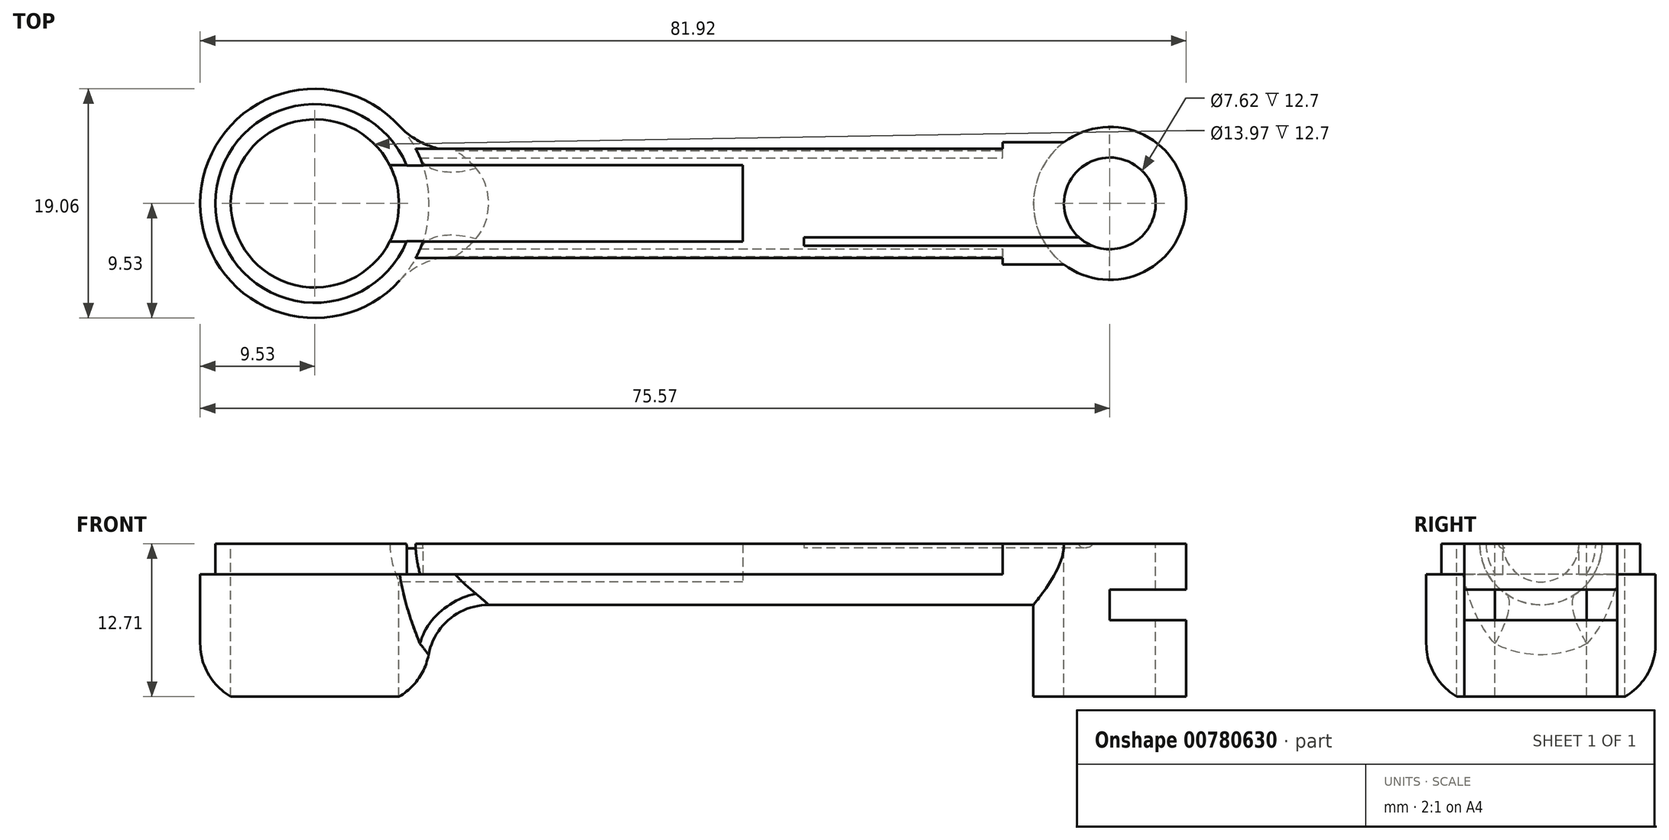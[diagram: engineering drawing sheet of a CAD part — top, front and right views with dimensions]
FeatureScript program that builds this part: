
annotation { "Feature Type Name" : "Feature", "Feature Type Description" : "" }
export const myFeature = defineFeature(function(context is Context, id is Id, definition is map)
    precondition{}
    {
        {
            var Q0;
            Q0=qCreatedBy(makeId("Top.planeOp"),FACE);
            var sketch = newSketch(context, id + "F0", { "sketchPlane" : qUnion([Q0])});
            skCircle(sketch, "E0", {"center": v(0, 0) * mm, "radius": 9.53 * mm});
            skSolve(sketch);
        }
        {
            var Q0;
            Q0=makeQuery(id+"F0.imprint","IMPRINT",FACE,{"disambiguationData":[TD([[makeQuery(id+"F0.imprint","IMPRINT",EDGE,{"derivedFrom":sQuery(id+"F0.wireOp",EDGE,"E0")}),1.0]])]});
            extrude(context, id + "F1", {"entities" : qUnion([Q0]), "depth" : 25.4 * mm, "offsetDistance" : 25.4 * mm});
        }
        {
            var Q0;
            Q0=makeQuery(id+"F1.opExtrude","CAP_FACE",FACE,{"disambiguationData":[OSD([sQuery(id+"F0.wireOp",EDGE,"E0")])],"isStart":false});
            var sketch = newSketch(context, id + "F2", { "sketchPlane" : qUnion([Q0])});
            skCircle(sketch, "E1", {"center": v(0, 0) * mm, "radius": 6.99 * mm});
            skSolve(sketch);
        }
        {
            var Q0;
            Q0=qCreatedBy(makeId("Right.planeOp"),FACE);
            var sketch = newSketch(context, id + "F3", { "sketchPlane" : qUnion([Q0])});
            skCircle(sketch, "E2", {"center": v(0, 15.88) * mm, "radius": 3.18 * mm});
            skSolve(sketch);
        }
        {
            var Q0;
            Q0=qSketchRegion(id+"F3",true);
            extrude(context, id + "F4", {"entities" : qUnion([Q0]), "operationType" : NewBodyOperationType.REMOVE, "depth" : 12.7 * mm, "offsetDistance" : 25.4 * mm});
        }
        {
            var Q0;
            Q0=qCreatedBy(makeId("Right.planeOp"),FACE);
            var sketch = newSketch(context, id + "F5", { "sketchPlane" : qUnion([Q0])});
            skLineSegment(sketch, "E3.top", {"start": v(9.53, 15.88) * mm, "end": v(-9.53, 15.88) * mm});
            skPoint(sketch, "E3.middle", {"position": v(0, 7.94) * mm});
            skLineSegment(sketch, "E4", {"start": v(-9.53, 15.88) * mm, "end": v(-9.53, 28.58) * mm});
            skLineSegment(sketch, "E5", {"start": v(9.53, 15.88) * mm, "end": v(9.53, 28.58) * mm});
            skLineSegment(sketch, "E6", {"start": v(-9.53, 28.58) * mm, "end": v(9.53, 28.58) * mm});
            skSolve(sketch);
        }
        {
            var Q0;
            Q0=qSketchRegion(id+"F5",true);
            extrude(context, id + "F6", {"entities" : qUnion([Q0]), "operationType" : NewBodyOperationType.REMOVE, "oppositeDirection" : true, "depth" : 25.4 * mm, "offsetDistance" : 25.4 * mm, "symmetric" : true});
        }
        {
            var Q0;
            Q0=qCreatedBy(makeId("Right.planeOp"),FACE);
            var sketch = newSketch(context, id + "F7", { "sketchPlane" : qUnion([Q0])});
            skArc(sketch, "E7", {"start": v(3.18, 15.88) * mm, "mid": v(0, 12.7) * mm, "end": v(-3.18, 15.88) * mm});
            skArc(sketch, "E8", {"start": v(-3.15, 18.42) * mm, "mid": v(-3.82, 17.22) * mm, "end": v(-4.05, 15.88) * mm});
            skArc(sketch, "E9", {"start": v(3.15, 18.42) * mm, "mid": v(3.82, 17.22) * mm, "end": v(4.05, 15.88) * mm});
            skLineSegment(sketch, "E10", {"start": v(-3.15, 18.42) * mm, "end": v(-4.4, 18.42) * mm});
            skLineSegment(sketch, "E11", {"start": v(3.15, 18.42) * mm, "end": v(4.4, 18.42) * mm});
            skLineSegment(sketch, "E12", {"start": v(-3.18, 15.88) * mm, "end": v(-4.05, 15.88) * mm});
            skLineSegment(sketch, "E13", {"start": v(3.18, 15.88) * mm, "end": v(4.05, 15.88) * mm});
            skArc(sketch, "E14", {"start": v(-4.4, 18.42) * mm, "mid": v(0, 10.8) * mm, "end": v(4.4, 18.42) * mm});
            skSolve(sketch);
        }
        {
            var Q0;
            Q0=qSketchRegion(id+"F7",true);
            var Q1;
            Q1=qConstructionFilter(qBodyType(qCreatedBy(id+"F7",EDGE),BodyType.WIRE),ConstructionObject.NO);
            extrude(context, id + "F8", {"entities" : qUnion([Q0]), "operationType" : NewBodyOperationType.ADD, "surfaceEntities" : qUnion([Q1]), "depth" : 38.1 * mm, "offsetDistance" : 25.4 * mm});
        }
        {
            var Q0;
            Q0=makeQuery(id+"F2.imprint","IMPRINT",FACE,{"disambiguationData":[TD([[makeQuery(id+"F2.imprint","IMPRINT",EDGE,{"derivedFrom":sQuery(id+"F2.wireOp",EDGE,"E1")}),1.0]])]});
            extrude(context, id + "F9", {"entities" : qUnion([Q0]), "operationType" : NewBodyOperationType.REMOVE, "oppositeDirection" : true, "depth" : 12.7 * mm, "offsetDistance" : 25.4 * mm});
        }
        {
            var Q0;
            Q0=makeQuery(id+"F8.opExtrude","CAP_FACE",FACE,{"disambiguationData":[OSD([sQuery(id+"F7.wireOp",EDGE,"E7"),sQuery(id+"F7.wireOp",EDGE,"E8"),sQuery(id+"F7.wireOp",EDGE,"E9"),sQuery(id+"F7.wireOp",EDGE,"E10"),sQuery(id+"F7.wireOp",EDGE,"E11"),sQuery(id+"F7.wireOp",EDGE,"E12"),sQuery(id+"F7.wireOp",EDGE,"E13"),sQuery(id+"F7.wireOp",EDGE,"E14")])],"isStart":false});
            var sketch = newSketch(context, id + "F10", { "sketchPlane" : qUnion([Q0])});
            skArc(sketch, "E15", {"start": v(-5.08, 15.88) * mm, "mid": v(0, 10.8) * mm, "end": v(5.08, 15.88) * mm});
            skArc(sketch, "E16", {"start": v(-3.53, 15.88) * mm, "mid": v(-3.18, 15.52) * mm, "end": v(-2.82, 15.88) * mm});
            skLineSegment(sketch, "E17", {"start": v(5.08, 15.88) * mm, "end": v(-2.82, 15.88) * mm});
            skLineSegment(sketch, "E18", {"start": v(-3.53, 15.88) * mm, "end": v(-5.08, 15.88) * mm});
            skSolve(sketch);
        }
        {
            var Q0;
            Q0=qSketchRegion(id+"F10",true);
            extrude(context, id + "F11", {"entities" : qUnion([Q0]), "operationType" : NewBodyOperationType.ADD, "depth" : 24.13 * mm, "offsetDistance" : 25.4 * mm});
        }
        {
            var Q0;
            Q0=makeQuery(id+"F1.opExtrude","CAP_FACE",FACE,{"disambiguationData":[OSD([sQuery(id+"F0.wireOp",EDGE,"E0")])],"isStart":true});
            var sketch = newSketch(context, id + "F12", { "sketchPlane" : qUnion([Q0])});
            skCircle(sketch, "E19", {"center": v(-3.18, 3.18) * mm, "radius": 0.95 * mm});
            skCircle(sketch, "E20", {"center": v(3.18, 3.18) * mm, "radius": 0.95 * mm});
            skCircle(sketch, "E21", {"center": v(3.18, -3.18) * mm, "radius": 0.95 * mm});
            skCircle(sketch, "E22", {"center": v(-3.18, -3.18) * mm, "radius": 0.95 * mm});
            skSolve(sketch);
        }
        {
            var Q0;
            Q0=qSketchRegion(id+"F12",true);
            extrude(context, id + "F13", {"entities" : qUnion([Q0]), "operationType" : NewBodyOperationType.REMOVE, "oppositeDirection" : true, "depth" : 25.4 * mm, "offsetDistance" : 25.4 * mm});
        }
        {
            var Q0;
            Q0=makeQuery(id+"F1.opExtrude","CAP_FACE",FACE,{"disambiguationData":[OSD([sQuery(id+"F0.wireOp",EDGE,"E0")])],"isStart":true});
            var sketch = newSketch(context, id + "F14", { "sketchPlane" : qUnion([Q0])});
            skCircle(sketch, "E23", {"center": v(0, 0) * mm, "radius": 6.99 * mm});
            skSolve(sketch);
        }
        {
            var Q0;
            Q0=qSketchRegion(id+"F14",true);
            extrude(context, id + "F15", {"entities" : qUnion([Q0]), "operationType" : NewBodyOperationType.REMOVE, "oppositeDirection" : true, "depth" : 7.62 * mm, "offsetDistance" : 25.4 * mm});
        }
        {
            var Q0;
            Q0=makeQuery(id+"F9.boolean.opBoolean","SPLIT",FACE,{"disambiguationData":[TD([makeQuery(id+"F1.opExtrude","SWEPT_FACE",FACE,{"disambiguationData":[OSD([sQuery(id+"F0.wireOp",EDGE,"E0")])]})])],"derivedFrom":makeQuery(id+"F8.boolean.opBoolean","MERGE",FACE,{"derivedFrom":[makeQuery(id+"F6.boolean.opBoolean","COPY",FACE,{"derivedFrom":makeQuery(id+"F6.opExtrude","SWEPT_FACE",FACE,{"disambiguationData":[OSD([sQuery(id+"F5.wireOp",EDGE,"E3.top")])]})}),makeQuery(id+"F8.opExtrude","SWEPT_FACE",FACE,{"disambiguationData":[OSD([sQuery(id+"F7.wireOp",EDGE,"E12")])]}),makeQuery(id+"F8.opExtrude","SWEPT_FACE",FACE,{"disambiguationData":[OSD([sQuery(id+"F7.wireOp",EDGE,"E13")])]})]})});
            var sketch = newSketch(context, id + "F16", { "sketchPlane" : qUnion([Q0])});
            skCircle(sketch, "E24", {"center": v(0, 0) * mm, "radius": 6.99 * mm});
            skCircle(sketch, "E25", {"center": v(0, 0) * mm, "radius": 8.26 * mm});
            skSolve(sketch);
        }
        {
            var Q0;
            Q0=qSketchRegion(id+"F16",true);
            extrude(context, id + "F17", {"entities" : qUnion([Q0]), "operationType" : NewBodyOperationType.REMOVE, "depth" : 25.4 * mm, "offsetDistance" : 25.4 * mm});
        }
        {
            var Q0;
            Q0=makeQuery(id+"F8.opExtrude","SWEPT_FACE",FACE,{"disambiguationData":[OSD([sQuery(id+"F7.wireOp",EDGE,"E11")])]});
            var sketch = newSketch(context, id + "F18", { "sketchPlane" : qUnion([Q0])});
            skArc(sketch, "E26", {"start": v(7.63, 3.15) * mm, "mid": v(-8.25, 0) * mm, "end": v(7.63, -3.15) * mm});
            skArc(sketch, "E27", {"start": v(8.99, 3.15) * mm, "mid": v(-9.53, 0) * mm, "end": v(8.99, -3.15) * mm});
            skLineSegment(sketch, "E28", {"start": v(7.63, 3.15) * mm, "end": v(8.99, 3.15) * mm});
            skLineSegment(sketch, "E29", {"start": v(7.63, -3.15) * mm, "end": v(8.99, -3.15) * mm});
            skSolve(sketch);
        }
        {
            var Q0;
            Q0=qSketchRegion(id+"F18",true);
            extrude(context, id + "F19", {"entities" : qUnion([Q0]), "operationType" : NewBodyOperationType.REMOVE, "oppositeDirection" : true, "depth" : 5.08 * mm, "offsetDistance" : 25.4 * mm});
        }
        {
            var Q0;
            {var subQ0=sQuery(id+"F7.wireOp",EDGE,"E10");var subQ1=sQuery(id+"F7.wireOp",EDGE,"E8");var subQ2=sQuery(id+"F7.wireOp",EDGE,"E12");var subQ3=sQuery(id+"F7.wireOp",EDGE,"E13");var subQ4=sQuery(id+"F7.wireOp",EDGE,"E14");Q0=makeQuery(id+"F11.boolean.opBoolean","SPLIT",FACE,{"disambiguationData":[TD([makeQuery(id+"F8.opExtrude","SWEPT_FACE",FACE,{"disambiguationData":[OSD([subQ1])]})])],"derivedFrom":makeQuery(id+"F8.opExtrude","CAP_FACE",FACE,{"disambiguationData":[OSD([sQuery(id+"F7.wireOp",EDGE,"E7"),subQ1,sQuery(id+"F7.wireOp",EDGE,"E9"),subQ0,sQuery(id+"F7.wireOp",EDGE,"E11"),subQ2,subQ3,subQ4])],"isStart":false})});}
            var sketch = newSketch(context, id + "F20", { "sketchPlane" : qUnion([Q0])});
            skArc(sketch, "E30", {"start": v(-4.05, 15.88) * mm, "mid": v(0, 19.92) * mm, "end": v(4.05, 15.88) * mm});
            skLineSegment(sketch, "E31", {"start": v(-4.05, 15.88) * mm, "end": v(4.05, 15.88) * mm});
            skSolve(sketch);
        }
        {
            var Q0;
            Q0=qSketchRegion(id+"F20",true);
            extrude(context, id + "F21", {"entities" : qUnion([Q0]), "operationType" : NewBodyOperationType.REMOVE, "oppositeDirection" : true, "depth" : 63.5 * mm, "offsetDistance" : 25.4 * mm});
        }
        {
            var Q0;
            {var subQ0=sQuery(id+"F7.wireOp",EDGE,"E10");var subQ1=sQuery(id+"F7.wireOp",EDGE,"E8");var subQ2=sQuery(id+"F7.wireOp",EDGE,"E12");var subQ3=sQuery(id+"F7.wireOp",EDGE,"E13");var subQ4=sQuery(id+"F7.wireOp",EDGE,"E14");Q0=makeQuery(id+"F11.boolean.opBoolean","SPLIT",FACE,{"disambiguationData":[TD([makeQuery(id+"F8.opExtrude","SWEPT_FACE",FACE,{"disambiguationData":[OSD([subQ1])]})])],"derivedFrom":makeQuery(id+"F8.opExtrude","CAP_FACE",FACE,{"disambiguationData":[OSD([sQuery(id+"F7.wireOp",EDGE,"E7"),subQ1,sQuery(id+"F7.wireOp",EDGE,"E9"),subQ0,sQuery(id+"F7.wireOp",EDGE,"E11"),subQ2,subQ3,subQ4])],"isStart":false})});}
            var sketch = newSketch(context, id + "F22", { "sketchPlane" : qUnion([Q0])});
            skArc(sketch, "E32", {"start": v(-3.78, 13.34) * mm, "mid": v(-4.35, 14.55) * mm, "end": v(-4.55, 15.88) * mm});
            skLineSegment(sketch, "E33", {"start": v(-3.78, 13.34) * mm, "end": v(-4.4, 13.34) * mm});
            skArc(sketch, "E34", {"start": v(-3.15, 18.42) * mm, "mid": v(-3.82, 17.22) * mm, "end": v(-4.05, 15.88) * mm});
            skLineSegment(sketch, "E35", {"start": v(-4.55, 15.88) * mm, "end": v(-4.05, 15.88) * mm});
            skLineSegment(sketch, "E36", {"start": v(-3.15, 18.42) * mm, "end": v(-4.4, 18.42) * mm});
            skArc(sketch, "E37", {"start": v(-4.4, 13.34) * mm, "mid": v(-5.08, 15.88) * mm, "end": v(-4.4, 18.42) * mm});
            skSolve(sketch);
        }
        {
            var Q0;
            Q0 = qSketchRegion(id + "F22", true);
            extrude(context, id + "F23", {"entities" : qUnion([Q0]), "operationType" : NewBodyOperationType.REMOVE, "oppositeDirection" : true, "depth" : 30.48 * mm, "offsetDistance" : 25.4 * mm});
        }
        {
            var Q0;
            {var subQ0=sQuery(id+"F7.wireOp",EDGE,"E11");var subQ1=sQuery(id+"F7.wireOp",EDGE,"E9");var subQ2=sQuery(id+"F7.wireOp",EDGE,"E12");var subQ3=sQuery(id+"F7.wireOp",EDGE,"E13");var subQ4=sQuery(id+"F7.wireOp",EDGE,"E14");Q0=makeQuery(id+"F11.boolean.opBoolean","SPLIT",FACE,{"disambiguationData":[TD([makeQuery(id+"F8.opExtrude","SWEPT_FACE",FACE,{"disambiguationData":[OSD([subQ1])]})])],"derivedFrom":makeQuery(id+"F8.opExtrude","CAP_FACE",FACE,{"disambiguationData":[OSD([sQuery(id+"F7.wireOp",EDGE,"E7"),sQuery(id+"F7.wireOp",EDGE,"E8"),subQ1,sQuery(id+"F7.wireOp",EDGE,"E10"),subQ0,subQ2,subQ3,subQ4])],"isStart":false})});}
            var sketch = newSketch(context, id + "F24", { "sketchPlane" : qUnion([Q0])});
            skArc(sketch, "E38", {"start": v(3.78, 13.34) * mm, "mid": v(4.35, 14.55) * mm, "end": v(4.55, 15.88) * mm});
            skLineSegment(sketch, "E39", {"start": v(4.55, 15.88) * mm, "end": v(4.05, 15.88) * mm});
            skArc(sketch, "E40", {"start": v(4.05, 15.88) * mm, "mid": v(3.82, 17.22) * mm, "end": v(3.15, 18.42) * mm});
            skLineSegment(sketch, "E41", {"start": v(3.15, 18.42) * mm, "end": v(4.4, 18.42) * mm});
            skLineSegment(sketch, "E42", {"start": v(3.78, 13.34) * mm, "end": v(4.4, 13.34) * mm});
            skArc(sketch, "E43", {"start": v(4.4, 13.34) * mm, "mid": v(5.08, 15.88) * mm, "end": v(4.4, 18.42) * mm});
            skSolve(sketch);
        }
        {
            var Q0;
            Q0 = qSketchRegion(id + "F24", true);
            extrude(context, id + "F25", {"entities" : qUnion([Q0]), "operationType" : NewBodyOperationType.REMOVE, "oppositeDirection" : true, "depth" : 30.48 * mm, "offsetDistance" : 25.4 * mm});
        }
        {
            var Q0;
            Q0=qCreatedBy(makeId("Right.planeOp"),FACE);
            var sketch = newSketch(context, id + "F26", { "sketchPlane" : qUnion([Q0])});
            skLineSegment(sketch, "E44.bottom", {"start": v(-9.53, 0) * mm, "end": v(9.53, 0) * mm});
            skLineSegment(sketch, "E44.top", {"start": v(-9.53, 3.17) * mm, "end": v(9.53, 3.17) * mm});
            skLineSegment(sketch, "E44.left", {"start": v(-9.53, 0) * mm, "end": v(-9.53, 3.17) * mm});
            skLineSegment(sketch, "E44.right", {"start": v(9.53, 0) * mm, "end": v(9.53, 3.17) * mm});
            skSolve(sketch);
        }
        {
            var Q0;
            Q0 = qSketchRegion(id + "F26", true);
            extrude(context, id + "F27", {"entities" : qUnion([Q0]), "operationType" : NewBodyOperationType.REMOVE, "oppositeDirection" : true, "depth" : 25.4 * mm, "offsetDistance" : 25.4 * mm, "symmetric" : true});
        }
        {
            var Q0;
            Q0=makeQuery(id+"F15.boolean.opBoolean","COPY",FACE,{"derivedFrom":makeQuery(id+"F15.opExtrude","CAP_FACE",FACE,{"disambiguationData":[OSD([sQuery(id+"F14.wireOp",EDGE,"E23")])],"isStart":false})});
            var sketch = newSketch(context, id + "F28", { "sketchPlane" : qUnion([Q0])});
            skCircle(sketch, "E45", {"center": v(0, 0) * mm, "radius": 6.99 * mm});
            skSolve(sketch);
        }
        {
            var Q0;
            Q0 = qSketchRegion(id + "F28", true);
            extrude(context, id + "F29", {"entities" : qUnion([Q0]), "operationType" : NewBodyOperationType.REMOVE, "oppositeDirection" : true, "depth" : 25.4 * mm, "offsetDistance" : 25.4 * mm});
        }
        {
            var Q0;
            Q0=makeQuery(id+"F27.boolean.opBoolean","INTERSECT",EDGE,{"derivedFrom":[makeQuery(id+"F1.opExtrude","SWEPT_FACE",FACE,{"disambiguationData":[OSD([sQuery(id+"F0.wireOp",EDGE,"E0")])]}),makeQuery(id+"F27.opExtrude","SWEPT_FACE",FACE,{"disambiguationData":[OSD([sQuery(id+"F26.wireOp",EDGE,"E44.top")])]})]});
            fillet(context, id + "F30", {"entities" : qUnion([Q0]), "radius" : 5.08 * mm, "tangentPropagation" : true, "allowEdgeOverflow" : false});
        }
        {
            var Q0;
            Q0=makeQuery(id+"F19.boolean.opBoolean","SPLIT",EDGE,{"derivedFrom":makeQuery(id+"F8.boolean.opBoolean","INTERSECT",EDGE,{"derivedFrom":[makeQuery(id+"F1.opExtrude","SWEPT_FACE",FACE,{"disambiguationData":[OSD([sQuery(id+"F0.wireOp",EDGE,"E0")])]}),makeQuery(id+"F8.opExtrude","SWEPT_FACE",FACE,{"disambiguationData":[OSD([sQuery(id+"F7.wireOp",EDGE,"E14")])]})]})});
            fillet(context, id + "F31", {"entities" : qUnion([Q0]), "radius" : 5.08 * mm, "tangentPropagation" : true, "allowEdgeOverflow" : false});
        }
        {
            var Q0;
            {var subQ0=sQuery(id+"F7.wireOp",EDGE,"E9");var subQ1=makeQuery(id+"F8.opExtrude","SWEPT_FACE",FACE,{"disambiguationData":[OSD([subQ0])]});var subQ2=sQuery(id+"F10.wireOp",EDGE,"aL0u9GlF-6Q7s-W1V7-4wS0-8lCQG8VcdnJv");var subQ3=sQuery(id+"F10.wireOp",EDGE,"2Tc0jqr0-cNR8-OvJQ-WwAY-mDO75ud9QsQn");var subQ7=sQuery(id+"F7.wireOp",EDGE,"E13");var subQ8=sQuery(id+"F7.wireOp",EDGE,"E12");var subQ9=sQuery(id+"F7.wireOp",EDGE,"E8");var subQ16=makeQuery(id+"F8.boolean.opBoolean","MERGE",FACE,{"derivedFrom":[makeQuery(id+"F6.boolean.opBoolean","COPY",FACE,{"derivedFrom":makeQuery(id+"F6.opExtrude","SWEPT_FACE",FACE,{"disambiguationData":[OSD([sQuery(id+"F5.wireOp",EDGE,"E3.top")])]})}),makeQuery(id+"F8.opExtrude","SWEPT_FACE",FACE,{"disambiguationData":[OSD([subQ8])]}),makeQuery(id+"F8.opExtrude","SWEPT_FACE",FACE,{"disambiguationData":[OSD([subQ7])]})]});Q0=makeQuery(id+"F25.boolean.opBoolean","MERGE",FACE,{"derivedFrom":[makeQuery(id+"F19.boolean.opBoolean","SPLIT",FACE,{"disambiguationData":[TD([subQ1])],"derivedFrom":makeQuery(id+"F17.boolean.opBoolean","MERGE",FACE,{"derivedFrom":[makeQuery(id+"F9.boolean.opBoolean","SPLIT",FACE,{"disambiguationData":[TD([makeQuery(id+"F1.opExtrude","SWEPT_FACE",FACE,{"disambiguationData":[OSD([sQuery(id+"F0.wireOp",EDGE,"E0")])]})])],"derivedFrom":subQ16}),makeQuery(id+"F11.boolean.opBoolean","MERGE",FACE,{"derivedFrom":[makeQuery(id+"F9.boolean.opBoolean","SPLIT",FACE,{"disambiguationData":[TD([makeQuery(id+"F8.opExtrude","SWEPT_FACE",FACE,{"disambiguationData":[OSD([subQ9])]})])],"derivedFrom":subQ16}),makeQuery(id+"F11.opExtrude","SWEPT_FACE",FACE,{"disambiguationData":[OSD([subQ2])]})]}),makeQuery(id+"F11.boolean.opBoolean","MERGE",FACE,{"derivedFrom":[makeQuery(id+"F9.boolean.opBoolean","SPLIT",FACE,{"disambiguationData":[TD([subQ1])],"derivedFrom":subQ16}),makeQuery(id+"F11.opExtrude","SWEPT_FACE",FACE,{"disambiguationData":[OSD([subQ3])]})]}),makeQuery(id+"F17.opExtrude","CAP_FACE",FACE,{"disambiguationData":[OSD([sQuery(id+"F16.wireOp",EDGE,"E24"),sQuery(id+"F16.wireOp",EDGE,"E25")])],"isStart":true})]})}),makeQuery(id+"F25.opExtrude","SWEPT_FACE",FACE,{"disambiguationData":[OSD([sQuery(id+"F24.wireOp",EDGE,"E39")])]})]});}
            var sketch = newSketch(context, id + "F32", { "sketchPlane" : qUnion([Q0])});
            skCircle(sketch, "E46", {"center": v(66.04, 0) * mm, "radius": 3.81 * mm});
            skCircle(sketch, "E47", {"center": v(66.04, 0) * mm, "radius": 6.35 * mm});
            skSolve(sketch);
        }
        {
            var Q0;
            Q0 = qSketchRegion(id + "F32", true);
            extrude(context, id + "F33", {"entities" : qUnion([Q0]), "operationType" : NewBodyOperationType.ADD, "oppositeDirection" : true, "depth" : 12.7 * mm, "offsetDistance" : 25.4 * mm});
        }
        {
            var Q0;
            Q0=makeQuery(id+"F11.opExtrude","CAP_FACE",FACE,{"disambiguationData":[OSD([sQuery(id+"F10.wireOp",EDGE,"E15"),sQuery(id+"F10.wireOp",EDGE,"00xkIltH-ur7c-vDCf-NMd2-okXEgH0ywGPR"),sQuery(id+"F10.wireOp",EDGE,"2Tc0jqr0-cNR8-OvJQ-WwAY-mDO75ud9QsQn"),sQuery(id+"F10.wireOp",EDGE,"aL0u9GlF-6Q7s-W1V7-4wS0-8lCQG8VcdnJv")])],"isStart":true});
            var sketch = newSketch(context, id + "F34", { "sketchPlane" : qUnion([Q0])});
            skArc(sketch, "E48", {"start": v(-3.18, 15.88) * mm, "mid": v(0, 12.7) * mm, "end": v(3.18, 15.88) * mm});
            skLineSegment(sketch, "E49", {"start": v(-3.18, 15.88) * mm, "end": v(3.18, 15.88) * mm});
            skSolve(sketch);
        }
        {
            var Q0;
            Q0 = qSketchRegion(id + "F34", true);
            extrude(context, id + "F35", {"entities" : qUnion([Q0]), "operationType" : NewBodyOperationType.ADD, "depth" : 2.54 * mm, "offsetDistance" : 25.4 * mm});
        }
        {
            var Q0;
            {var subQ0=sQuery(id+"F7.wireOp",EDGE,"E7");var subQ1=sQuery(id+"F7.wireOp",EDGE,"E12");var subQ4=sQuery(id+"F7.wireOp",EDGE,"E13");Q0=makeQuery(id+"F35.boolean.opBoolean","MERGE",FACE,{"derivedFrom":[makeQuery(id+"F11.boolean.opBoolean","SPLIT",FACE,{"disambiguationData":[TD([makeQuery(id+"F4.boolean.opBoolean","COPY",FACE,{"derivedFrom":makeQuery(id+"F4.opExtrude","SWEPT_FACE",FACE,{"disambiguationData":[OSD([sQuery(id+"F3.wireOp",EDGE,"E2")])]})})])],"derivedFrom":makeQuery(id+"F8.opExtrude","CAP_FACE",FACE,{"disambiguationData":[OSD([subQ0,sQuery(id+"F7.wireOp",EDGE,"E8"),sQuery(id+"F7.wireOp",EDGE,"E9"),sQuery(id+"F7.wireOp",EDGE,"E10"),sQuery(id+"F7.wireOp",EDGE,"E11"),subQ1,subQ4,sQuery(id+"F7.wireOp",EDGE,"E14")])],"isStart":false})}),makeQuery(id+"F35.opExtrude","CAP_FACE",FACE,{"disambiguationData":[OSD([sQuery(id+"F34.wireOp",EDGE,"E48"),sQuery(id+"F34.wireOp",EDGE,"E49")])],"isStart":true})]});}
            extrude(context, id + "F36", {"entities" : qUnion([Q0]), "operationType" : NewBodyOperationType.REMOVE, "depth" : 27.94 * mm, "offsetDistance" : 25.4 * mm});
        }
        {
            var Q0;
            Q0=makeQuery(id+"F23.boolean.opBoolean","COPY",FACE,{"derivedFrom":makeQuery(id+"F23.opExtrude","CAP_FACE",FACE,{"disambiguationData":[OSD([sQuery(id+"F22.wireOp",EDGE,"E32"),sQuery(id+"F22.wireOp",EDGE,"E33"),sQuery(id+"F22.wireOp",EDGE,"E34"),sQuery(id+"F22.wireOp",EDGE,"E35"),sQuery(id+"F22.wireOp",EDGE,"E36"),sQuery(id+"F22.wireOp",EDGE,"E37")])],"isStart":true})});
            extrude(context, id + "F37", {"entities" : qUnion([Q0]), "operationType" : NewBodyOperationType.REMOVE, "oppositeDirection" : true, "depth" : 19.05 * mm, "offsetDistance" : 25.4 * mm});
        }
        {
            var Q0;
            Q0=makeQuery(id+"F25.boolean.opBoolean","COPY",FACE,{"derivedFrom":makeQuery(id+"F25.opExtrude","CAP_FACE",FACE,{"disambiguationData":[OSD([sQuery(id+"F24.wireOp",EDGE,"E38"),sQuery(id+"F24.wireOp",EDGE,"E39"),sQuery(id+"F24.wireOp",EDGE,"E40"),sQuery(id+"F24.wireOp",EDGE,"E41"),sQuery(id+"F24.wireOp",EDGE,"E42"),sQuery(id+"F24.wireOp",EDGE,"E43")])],"isStart":true})});
            extrude(context, id + "F38", {"entities" : qUnion([Q0]), "operationType" : NewBodyOperationType.REMOVE, "oppositeDirection" : true, "depth" : 19.05 * mm, "offsetDistance" : 25.4 * mm});
        }
        {
            var Q0;
            {var subQ0=sQuery(id+"F7.wireOp",EDGE,"E9");var subQ1=makeQuery(id+"F8.opExtrude","SWEPT_FACE",FACE,{"disambiguationData":[OSD([subQ0])]});var subQ2=sQuery(id+"F10.wireOp",EDGE,"E18");var subQ3=sQuery(id+"F10.wireOp",EDGE,"E17");var subQ8=sQuery(id+"F7.wireOp",EDGE,"E13");var subQ9=sQuery(id+"F7.wireOp",EDGE,"E12");var subQ10=sQuery(id+"F7.wireOp",EDGE,"E8");var subQ20=makeQuery(id+"F8.boolean.opBoolean","MERGE",FACE,{"derivedFrom":[makeQuery(id+"F6.boolean.opBoolean","COPY",FACE,{"derivedFrom":makeQuery(id+"F6.opExtrude","SWEPT_FACE",FACE,{"disambiguationData":[OSD([sQuery(id+"F5.wireOp",EDGE,"E3.top")])]})}),makeQuery(id+"F8.opExtrude","SWEPT_FACE",FACE,{"disambiguationData":[OSD([subQ9])]}),makeQuery(id+"F8.opExtrude","SWEPT_FACE",FACE,{"disambiguationData":[OSD([subQ8])]})]});var subQ21=makeQuery(id+"F8.opExtrude","SWEPT_FACE",FACE,{"disambiguationData":[OSD([subQ10])]});var subQ22=makeQuery(id+"F17.boolean.opBoolean","MERGE",FACE,{"derivedFrom":[makeQuery(id+"F9.boolean.opBoolean","SPLIT",FACE,{"disambiguationData":[TD([makeQuery(id+"F1.opExtrude","SWEPT_FACE",FACE,{"disambiguationData":[OSD([sQuery(id+"F0.wireOp",EDGE,"E0")])]})])],"derivedFrom":subQ20}),makeQuery(id+"F11.boolean.opBoolean","MERGE",FACE,{"derivedFrom":[makeQuery(id+"F9.boolean.opBoolean","SPLIT",FACE,{"disambiguationData":[TD([subQ21])],"derivedFrom":subQ20}),makeQuery(id+"F11.opExtrude","SWEPT_FACE",FACE,{"disambiguationData":[OSD([subQ2])]})]}),makeQuery(id+"F11.boolean.opBoolean","MERGE",FACE,{"derivedFrom":[makeQuery(id+"F9.boolean.opBoolean","SPLIT",FACE,{"disambiguationData":[TD([subQ1])],"derivedFrom":subQ20}),makeQuery(id+"F11.opExtrude","SWEPT_FACE",FACE,{"disambiguationData":[OSD([subQ3])]})]}),makeQuery(id+"F17.opExtrude","CAP_FACE",FACE,{"disambiguationData":[OSD([sQuery(id+"F16.wireOp",EDGE,"E24"),sQuery(id+"F16.wireOp",EDGE,"E25")])],"isStart":true})]});Q0=makeQuery(id+"F35.boolean.opBoolean","MERGE",FACE,{"derivedFrom":[makeQuery(id+"F33.boolean.opBoolean","MERGE",FACE,{"derivedFrom":[makeQuery(id+"F23.boolean.opBoolean","MERGE",FACE,{"derivedFrom":[makeQuery(id+"F19.boolean.opBoolean","SPLIT",FACE,{"disambiguationData":[TD([subQ21])],"derivedFrom":subQ22}),makeQuery(id+"F23.opExtrude","SWEPT_FACE",FACE,{"disambiguationData":[OSD([sQuery(id+"F22.wireOp",EDGE,"E35")])]})]}),makeQuery(id+"F25.boolean.opBoolean","MERGE",FACE,{"derivedFrom":[makeQuery(id+"F19.boolean.opBoolean","SPLIT",FACE,{"disambiguationData":[TD([subQ1])],"derivedFrom":subQ22}),makeQuery(id+"F25.opExtrude","SWEPT_FACE",FACE,{"disambiguationData":[OSD([sQuery(id+"F24.wireOp",EDGE,"E39")])]})]}),makeQuery(id+"F33.opExtrude","CAP_FACE",FACE,{"disambiguationData":[OSD([sQuery(id+"F32.wireOp",EDGE,"E46"),sQuery(id+"F32.wireOp",EDGE,"E47")])],"isStart":true})]}),makeQuery(id+"F35.opExtrude","SWEPT_FACE",FACE,{"disambiguationData":[OSD([sQuery(id+"F34.wireOp",EDGE,"E49")])]})]});}
            var sketch = newSketch(context, id + "F39", { "sketchPlane" : qUnion([Q0])});
            skArc(sketch, "E50", {"start": v(66.04, 6.35) * mm, "mid": v(72.39, 0) * mm, "end": v(66.04, -6.35) * mm});
            skLineSegment(sketch, "E51", {"start": v(66.04, 6.35) * mm, "end": v(66.04, -6.35) * mm});
            skSolve(sketch);
        }
        {
            var Q0;
            Q0 = qSketchRegion(id + "F39", true);
            extrude(context, id + "F40", {"entities" : qUnion([Q0]), "operationType" : NewBodyOperationType.REMOVE, "oppositeDirection" : true, "depth" : 6.35 * mm, "offsetDistance" : 25.4 * mm});
        }
        {
            var Q0;
            {var subQ0=sQuery(id+"F7.wireOp",EDGE,"E9");var subQ1=makeQuery(id+"F8.opExtrude","SWEPT_FACE",FACE,{"disambiguationData":[OSD([subQ0])]});var subQ2=sQuery(id+"F10.wireOp",EDGE,"E18");var subQ3=sQuery(id+"F10.wireOp",EDGE,"E17");var subQ8=sQuery(id+"F7.wireOp",EDGE,"E13");var subQ9=sQuery(id+"F7.wireOp",EDGE,"E12");var subQ10=sQuery(id+"F7.wireOp",EDGE,"E8");var subQ20=makeQuery(id+"F8.boolean.opBoolean","MERGE",FACE,{"derivedFrom":[makeQuery(id+"F6.boolean.opBoolean","COPY",FACE,{"derivedFrom":makeQuery(id+"F6.opExtrude","SWEPT_FACE",FACE,{"disambiguationData":[OSD([sQuery(id+"F5.wireOp",EDGE,"E3.top")])]})}),makeQuery(id+"F8.opExtrude","SWEPT_FACE",FACE,{"disambiguationData":[OSD([subQ9])]}),makeQuery(id+"F8.opExtrude","SWEPT_FACE",FACE,{"disambiguationData":[OSD([subQ8])]})]});var subQ21=makeQuery(id+"F8.opExtrude","SWEPT_FACE",FACE,{"disambiguationData":[OSD([subQ10])]});var subQ22=makeQuery(id+"F17.boolean.opBoolean","MERGE",FACE,{"derivedFrom":[makeQuery(id+"F9.boolean.opBoolean","SPLIT",FACE,{"disambiguationData":[TD([makeQuery(id+"F1.opExtrude","SWEPT_FACE",FACE,{"disambiguationData":[OSD([sQuery(id+"F0.wireOp",EDGE,"E0")])]})])],"derivedFrom":subQ20}),makeQuery(id+"F11.boolean.opBoolean","MERGE",FACE,{"derivedFrom":[makeQuery(id+"F9.boolean.opBoolean","SPLIT",FACE,{"disambiguationData":[TD([subQ21])],"derivedFrom":subQ20}),makeQuery(id+"F11.opExtrude","SWEPT_FACE",FACE,{"disambiguationData":[OSD([subQ2])]})]}),makeQuery(id+"F11.boolean.opBoolean","MERGE",FACE,{"derivedFrom":[makeQuery(id+"F9.boolean.opBoolean","SPLIT",FACE,{"disambiguationData":[TD([subQ1])],"derivedFrom":subQ20}),makeQuery(id+"F11.opExtrude","SWEPT_FACE",FACE,{"disambiguationData":[OSD([subQ3])]})]}),makeQuery(id+"F17.opExtrude","CAP_FACE",FACE,{"disambiguationData":[OSD([sQuery(id+"F16.wireOp",EDGE,"E24"),sQuery(id+"F16.wireOp",EDGE,"E25")])],"isStart":true})]});Q0=makeQuery(id+"F35.boolean.opBoolean","MERGE",FACE,{"derivedFrom":[makeQuery(id+"F33.boolean.opBoolean","MERGE",FACE,{"derivedFrom":[makeQuery(id+"F23.boolean.opBoolean","MERGE",FACE,{"derivedFrom":[makeQuery(id+"F19.boolean.opBoolean","SPLIT",FACE,{"disambiguationData":[TD([subQ21])],"derivedFrom":subQ22}),makeQuery(id+"F23.opExtrude","SWEPT_FACE",FACE,{"disambiguationData":[OSD([sQuery(id+"F22.wireOp",EDGE,"E35")])]})]}),makeQuery(id+"F25.boolean.opBoolean","MERGE",FACE,{"derivedFrom":[makeQuery(id+"F19.boolean.opBoolean","SPLIT",FACE,{"disambiguationData":[TD([subQ1])],"derivedFrom":subQ22}),makeQuery(id+"F25.opExtrude","SWEPT_FACE",FACE,{"disambiguationData":[OSD([sQuery(id+"F24.wireOp",EDGE,"E39")])]})]}),makeQuery(id+"F33.opExtrude","CAP_FACE",FACE,{"disambiguationData":[OSD([sQuery(id+"F32.wireOp",EDGE,"E46"),sQuery(id+"F32.wireOp",EDGE,"E47")])],"isStart":true})]}),makeQuery(id+"F35.opExtrude","SWEPT_FACE",FACE,{"disambiguationData":[OSD([sQuery(id+"F34.wireOp",EDGE,"E49")])]})]});}
            var sketch = newSketch(context, id + "F41", { "sketchPlane" : qUnion([Q0])});
            skArc(sketch, "E52", {"start": v(64.58, 6.18) * mm, "mid": v(72.39, -0.02) * mm, "end": v(64.53, -6.17) * mm});
            skArc(sketch, "E53", {"start": v(65.21, 3.72) * mm, "mid": v(69.85, 0.08) * mm, "end": v(65.36, -3.75) * mm});
            skLineSegment(sketch, "E54", {"start": v(65.21, 3.72) * mm, "end": v(64.58, 6.18) * mm});
            skLineSegment(sketch, "E55", {"start": v(65.36, -3.75) * mm, "end": v(64.53, -6.17) * mm});
            skSolve(sketch);
        }
        {
            var Q0;
            Q0 = qSketchRegion(id + "F41", true);
            extrude(context, id + "F42", {"entities" : qUnion([Q0]), "operationType" : NewBodyOperationType.ADD, "oppositeDirection" : true, "depth" : 3.8 * mm, "offsetDistance" : 25.4 * mm});
        }
        {
            var Q0;
            {var subQ0=sQuery(id+"F7.wireOp",EDGE,"E7");var subQ1=sQuery(id+"F7.wireOp",EDGE,"E12");var subQ4=sQuery(id+"F7.wireOp",EDGE,"E13");Q0=makeQuery(id+"F35.boolean.opBoolean","MERGE",FACE,{"derivedFrom":[makeQuery(id+"F11.boolean.opBoolean","SPLIT",FACE,{"disambiguationData":[TD([makeQuery(id+"F4.boolean.opBoolean","COPY",FACE,{"derivedFrom":makeQuery(id+"F4.opExtrude","SWEPT_FACE",FACE,{"disambiguationData":[OSD([sQuery(id+"F3.wireOp",EDGE,"E2")])]})})])],"derivedFrom":makeQuery(id+"F8.opExtrude","CAP_FACE",FACE,{"disambiguationData":[OSD([subQ0,sQuery(id+"F7.wireOp",EDGE,"E8"),sQuery(id+"F7.wireOp",EDGE,"E9"),sQuery(id+"F7.wireOp",EDGE,"E10"),sQuery(id+"F7.wireOp",EDGE,"E11"),subQ1,subQ4,sQuery(id+"F7.wireOp",EDGE,"E14")])],"isStart":false})}),makeQuery(id+"F35.opExtrude","CAP_FACE",FACE,{"disambiguationData":[OSD([sQuery(id+"F34.wireOp",EDGE,"E48"),sQuery(id+"F34.wireOp",EDGE,"E49")])],"isStart":true})]});}
            extrude(context, id + "F43", {"entities" : qUnion([Q0]), "operationType" : NewBodyOperationType.ADD, "depth" : 2.54 * mm, "offsetDistance" : 25.4 * mm});
        }
    });
